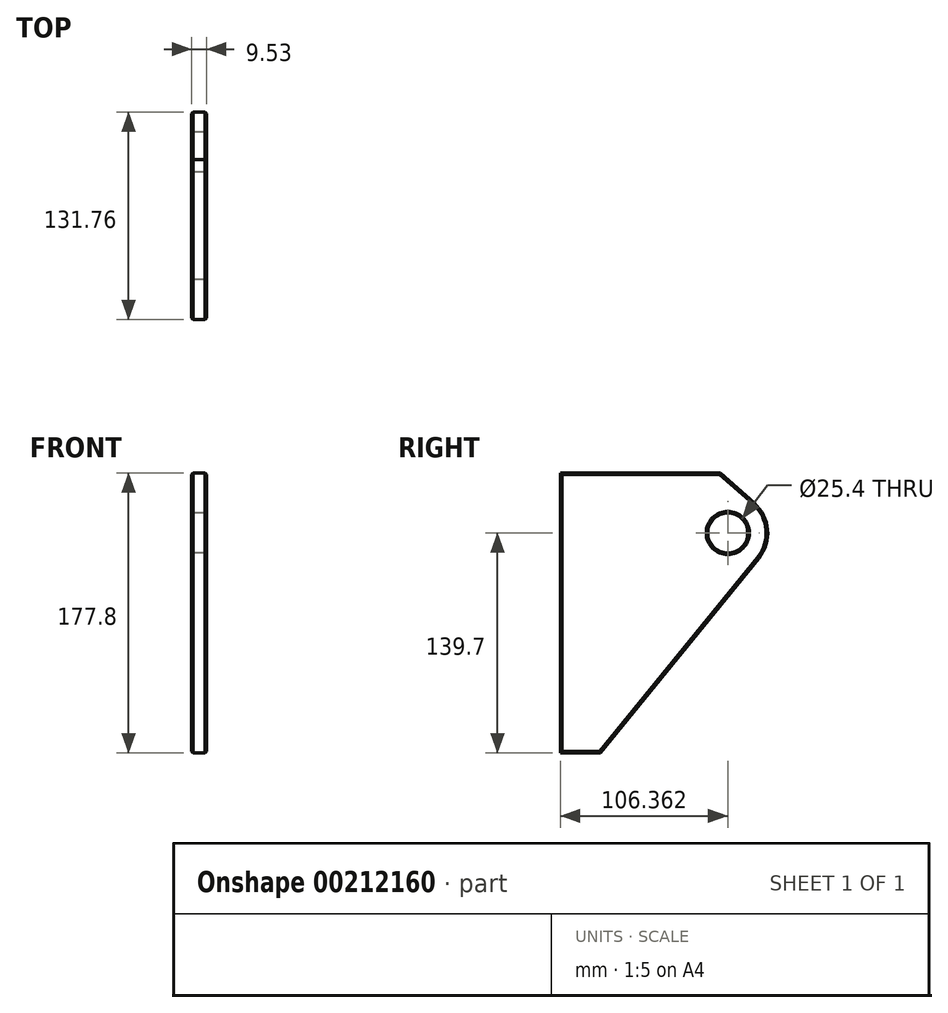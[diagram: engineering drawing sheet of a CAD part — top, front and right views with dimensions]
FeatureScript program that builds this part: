
annotation { "Feature Type Name" : "Feature", "Feature Type Description" : "" }
export const myFeature = defineFeature(function(context is Context, id is Id, definition is map)
    precondition{}
    {
        {
            var Q0;
            Q0=qCreatedBy(makeId("Right.planeOp"),FACE);
            var sketch = newSketch(context, id + "F0", { "sketchPlane" : qUnion([Q0])});
            skLineSegment(sketch, "E0", {"start": v(0, 0) * mm, "end": v(0, 177.8) * mm});
            skLineSegment(sketch, "E1", {"start": v(0, 177.8) * mm, "end": v(101.6, 177.8) * mm});
            skLineSegment(sketch, "E2", {"start": v(25.4, 0) * mm, "end": v(0, 0) * mm});
            skCircle(sketch, "E3", {"center": v(106.36, 139.7) * mm, "radius": 12.7 * mm});
            skLineSegment(sketch, "E4", {"start": v(25.4, 0) * mm, "end": v(126.06, 123.67) * mm});
            skLineSegment(sketch, "E5", {"start": v(101.6, 177.8) * mm, "end": v(123.18, 158.74) * mm});
            skArc(sketch, "E6", {"start": v(126.06, 123.67) * mm, "mid": v(131.68, 141.78) * mm, "end": v(123.18, 158.74) * mm});
            skSolve(sketch);
        }
        {
            var Q0;
            Q0=makeQuery(id+"F0.imprint","IMPRINT",FACE,{"disambiguationData":[TD([[makeQuery(id+"F0.imprint","IMPRINT",EDGE,{"derivedFrom":sQuery(id+"F0.wireOp",EDGE,"E0")}),-1.0]])]});
            extrude(context, id + "F1", {"entities" : qUnion([Q0]), "depth" : 9.52 * mm});
        }
        {
            var Q0;
            Q0=makeQuery(id+"F1.opExtrude","CAP_FACE",FACE,{"disambiguationData":[OSD([sQuery(id+"F0.wireOp",EDGE,"E0"),sQuery(id+"F0.wireOp",EDGE,"E1"),sQuery(id+"F0.wireOp",EDGE,"E2"),sQuery(id+"F0.wireOp",EDGE,"E3"),sQuery(id+"F0.wireOp",EDGE,"E4"),sQuery(id+"F0.wireOp",EDGE,"E5"),sQuery(id+"F0.wireOp",EDGE,"E6")])],"isStart":false});
            var Q1;
            Q1=makeQuery(id+"F1.opExtrude","CAP_FACE",FACE,{"disambiguationData":[OSD([sQuery(id+"F0.wireOp",EDGE,"E0"),sQuery(id+"F0.wireOp",EDGE,"E1"),sQuery(id+"F0.wireOp",EDGE,"E2"),sQuery(id+"F0.wireOp",EDGE,"E3"),sQuery(id+"F0.wireOp",EDGE,"E4"),sQuery(id+"F0.wireOp",EDGE,"E5"),sQuery(id+"F0.wireOp",EDGE,"E6")])],"isStart":true});
            chamfer(context, id + "F2", {"entities" : qUnion([Q0, Q1]), "width" : 1.02 * mm, "tangentPropagation" : true});
        }
    });
